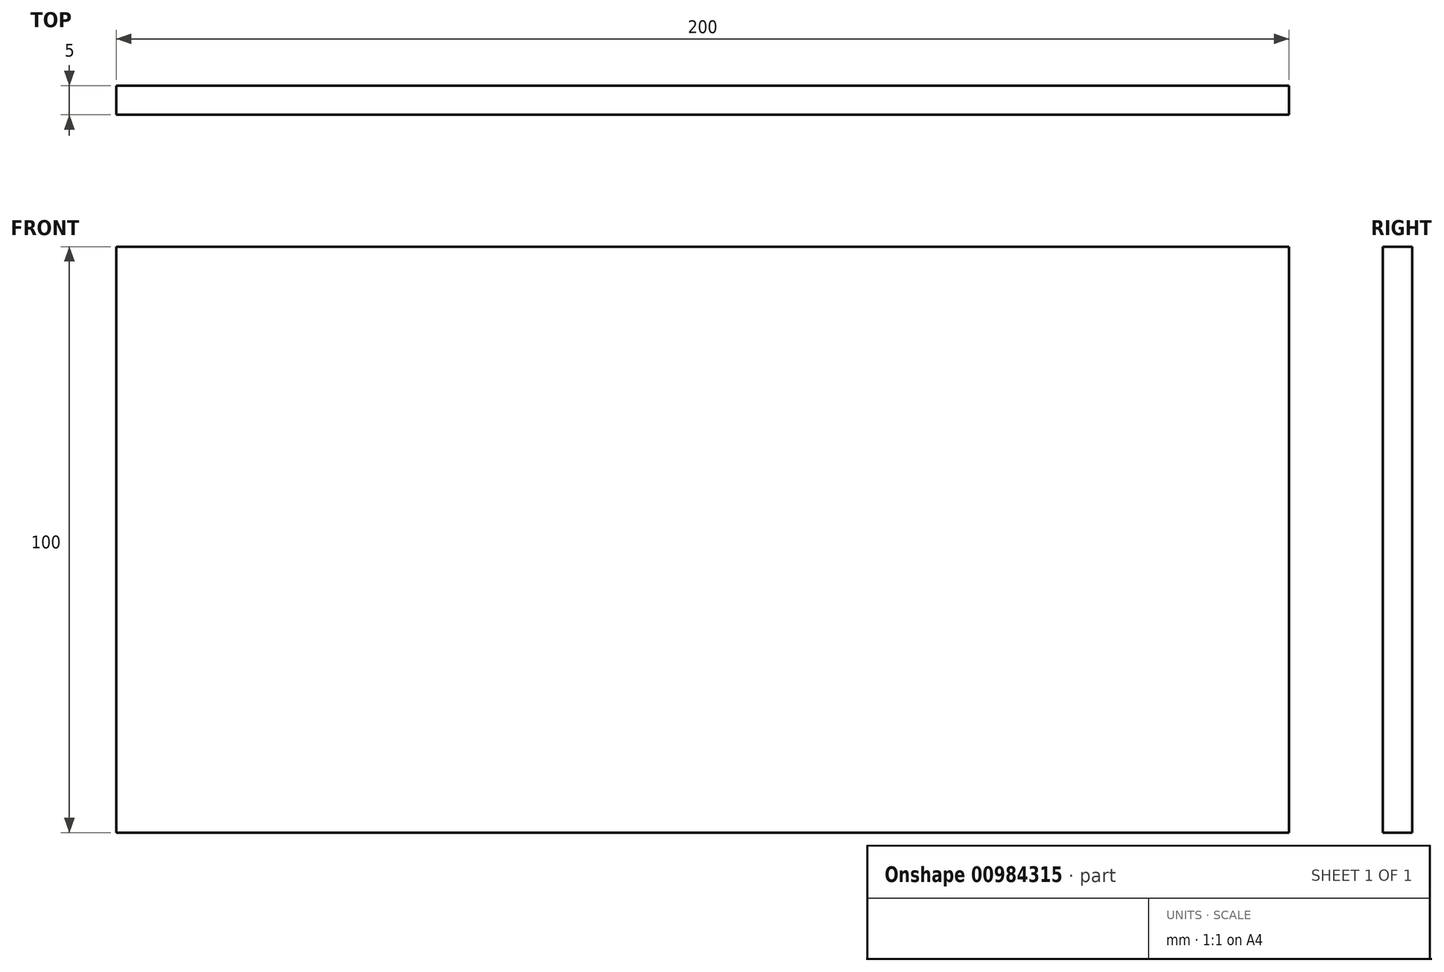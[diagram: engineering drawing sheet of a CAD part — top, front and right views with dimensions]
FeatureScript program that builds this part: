
annotation { "Feature Type Name" : "Feature", "Feature Type Description" : "" }
export const myFeature = defineFeature(function(context is Context, id is Id, definition is map)
    precondition{}
    {
        {
            var Q0;
            Q0=qCreatedBy(makeId("Front.planeOp"),FACE);
            var sketch = newSketch(context, id + "F0", { "sketchPlane" : qUnion([Q0])});
            skLineSegment(sketch, "E0.bottom", {"start": v(100, 50) * mm, "end": v(-100, 50) * mm});
            skLineSegment(sketch, "E0.top", {"start": v(100, -50) * mm, "end": v(-100, -50) * mm});
            skLineSegment(sketch, "E0.left", {"start": v(100, 50) * mm, "end": v(100, -50) * mm});
            skLineSegment(sketch, "E0.right", {"start": v(-100, 50) * mm, "end": v(-100, -50) * mm});
            skPoint(sketch, "E0.middle", {"position": v(0, 0) * mm});
            skSolve(sketch);
        }
        {
            var Q0;
            Q0=makeQuery(id+"F0.imprint","IMPRINT",FACE,{"disambiguationData":[TD([[makeQuery(id+"F0.imprint","IMPRINT",EDGE,{"derivedFrom":sQuery(id+"F0.wireOp",EDGE,"E0.bottom")}),1.0]])]});
            extrude(context, id + "F1", {"entities" : qUnion([Q0]), "depth" : 5 * mm, "offsetDistance" : 25 * mm});
        }
    });
